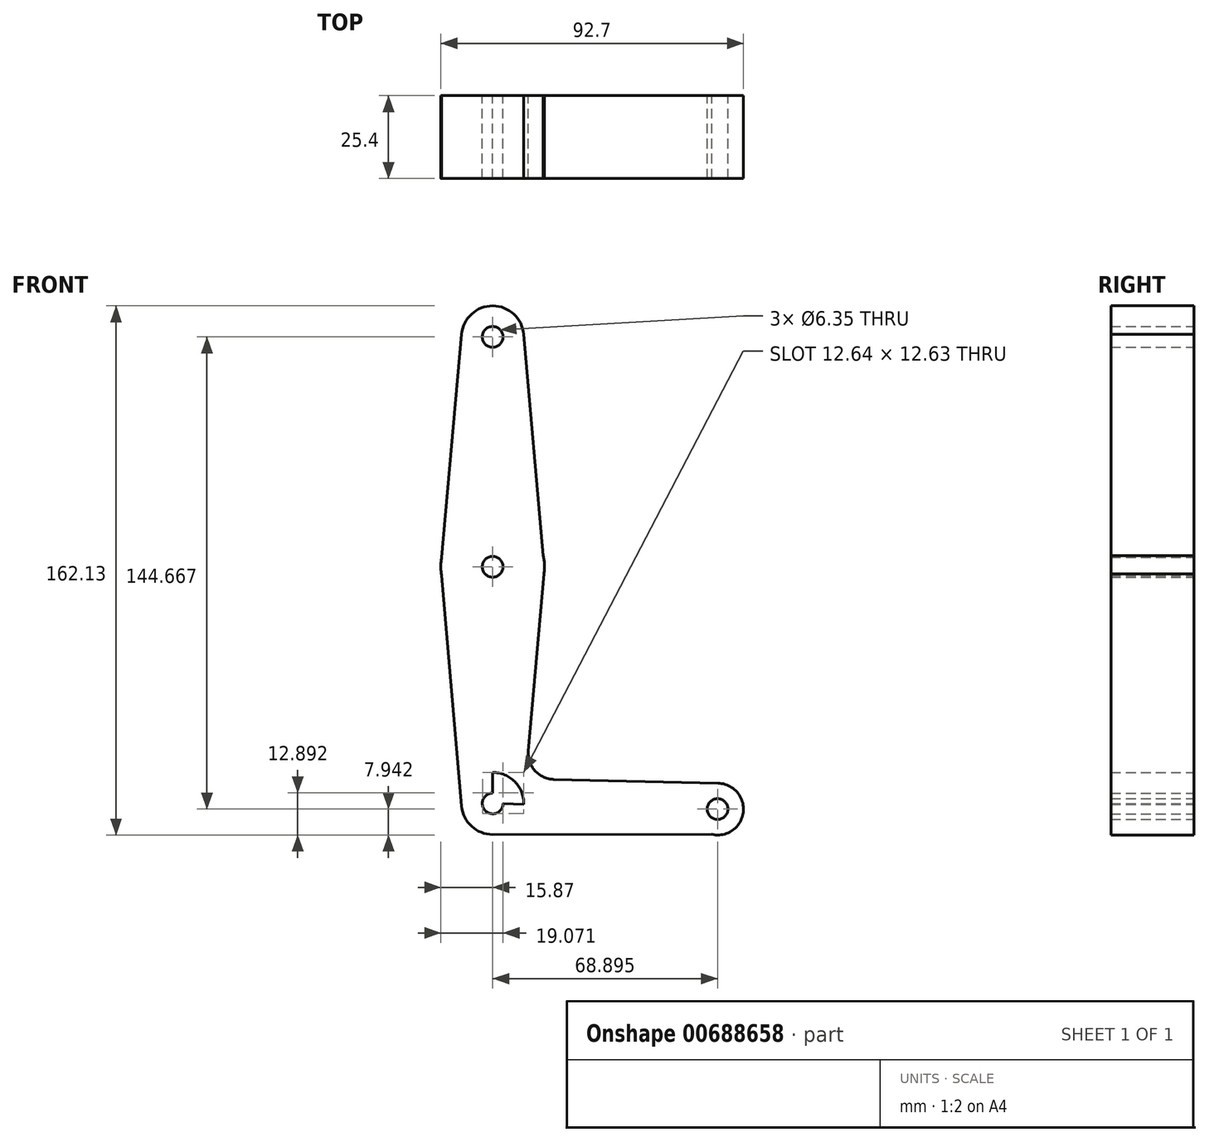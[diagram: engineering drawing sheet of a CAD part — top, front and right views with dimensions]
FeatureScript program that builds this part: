
annotation { "Feature Type Name" : "Feature", "Feature Type Description" : "" }
export const myFeature = defineFeature(function(context is Context, id is Id, definition is map)
    precondition{}
    {
        {
            var Q0;
            Q0=qCreatedBy(makeId("Front.planeOp"),FACE);
            var sketch = newSketch(context, id + "F0", { "sketchPlane" : qUnion([Q0])});
            skLineSegment(sketch, "E0", {"start": v(0, -72.52) * mm, "end": v(0, 70.4) * mm});
            skLineSegment(sketch, "E1", {"start": v(0, 70.4) * mm, "end": v(0, -72.52) * mm});
            skLineSegment(sketch, "E2", {"start": v(68.9, -74.26) * mm, "end": v(0, -72.52) * mm});
            skCircle(sketch, "E3", {"center": v(0, 70.4) * mm, "radius": 9.53 * mm});
            skCircle(sketch, "E4", {"center": v(0, 0) * mm, "radius": 15.88 * mm});
            skCircle(sketch, "E5", {"center": v(0, -72.52) * mm, "radius": 9.53 * mm});
            skCircle(sketch, "E6", {"center": v(68.9, -74.26) * mm, "radius": 7.94 * mm});
            skLineSegment(sketch, "E7", {"start": v(-9.48, 71.3) * mm, "end": v(-15.87, 0) * mm});
            skLineSegment(sketch, "E8", {"start": v(9.5, 71.15) * mm, "end": v(15.86, -0.58) * mm});
            skLineSegment(sketch, "E9", {"start": v(-15.87, 0) * mm, "end": v(-9.49, -73.34) * mm});
            skLineSegment(sketch, "E10", {"start": v(15.86, -0.58) * mm, "end": v(10.95, -56.5) * mm});
            skLineSegment(sketch, "E11", {"start": v(69.01, -66.32) * mm, "end": v(18.68, -65.14) * mm});
            skLineSegment(sketch, "E12", {"start": v(70.6, -82.01) * mm, "end": v(0, -82.04) * mm});
            skArc(sketch, "E13.filletArc", {"start": v(10.95, -56.5) * mm, "mid": v(12.94, -62.49) * mm, "end": v(18.68, -65.14) * mm});
            skCircle(sketch, "E14", {"center": v(0, 70.4) * mm, "radius": 3.18 * mm});
            skCircle(sketch, "E15", {"center": v(0, 0) * mm, "radius": 3.18 * mm});
            skCircle(sketch, "E16", {"center": v(0, -72.52) * mm, "radius": 3.18 * mm});
            skCircle(sketch, "E17", {"center": v(68.9, -74.26) * mm, "radius": 3.18 * mm});
            skText(sketch, "E18", { "text": "james collins, pd.1, 7.493", "fontName": "OpenSans-Regular.ttf"});
            const initialGuessF0  = {"E18": [0.05465, 0.06403, 1, 0, 0.02398]};
            skSetInitialGuess(sketch, initialGuessF0);
            skSolve(sketch);
        }
        {
            var Q0;
            Q0 = qSketchRegion(id + "F0", true);
            extrude(context, id + "F1", {"entities" : qUnion([Q0]), "depth" : 25.4 * mm, "offsetDistance" : 25.4 * mm});
        }
        {
            var Q0;
            Q0=makeQuery(id+"F1.opExtrude","SWEPT_BODY",BODY,{"disambiguationData":[OSD([sQuery(id+"F0.wireOp",EDGE,"E18.sketch_text.stroke-297"),sQuery(id+"F0.wireOp",EDGE,"E18.sketch_text.stroke-298"),sQuery(id+"F0.wireOp",EDGE,"E18.sketch_text.stroke-299"),sQuery(id+"F0.wireOp",EDGE,"E18.sketch_text.stroke-300"),sQuery(id+"F0.wireOp",EDGE,"E18.sketch_text.stroke-301"),sQuery(id+"F0.wireOp",EDGE,"E18.sketch_text.stroke-302"),sQuery(id+"F0.wireOp",EDGE,"E18.sketch_text.stroke-303"),sQuery(id+"F0.wireOp",EDGE,"E18.sketch_text.stroke-304")])]});
            deleteBodies(context, id + "F2", {"entities" : qUnion([Q0])});
        }
        {
            var Q0;
            Q0=makeQuery(id+"F1.opExtrude","SWEPT_BODY",BODY,{"disambiguationData":[OSD([sQuery(id+"F0.wireOp",EDGE,"E18.sketch_text.stroke-305"),sQuery(id+"F0.wireOp",EDGE,"E18.sketch_text.stroke-306"),sQuery(id+"F0.wireOp",EDGE,"E18.sketch_text.stroke-307"),sQuery(id+"F0.wireOp",EDGE,"E18.sketch_text.stroke-308"),sQuery(id+"F0.wireOp",EDGE,"E18.sketch_text.stroke-309"),sQuery(id+"F0.wireOp",EDGE,"E18.sketch_text.stroke-310"),sQuery(id+"F0.wireOp",EDGE,"E18.sketch_text.stroke-311"),sQuery(id+"F0.wireOp",EDGE,"E18.sketch_text.stroke-312"),sQuery(id+"F0.wireOp",EDGE,"E18.sketch_text.stroke-313"),sQuery(id+"F0.wireOp",EDGE,"E18.sketch_text.stroke-314"),sQuery(id+"F0.wireOp",EDGE,"E18.sketch_text.stroke-315"),sQuery(id+"F0.wireOp",EDGE,"E18.sketch_text.stroke-316"),sQuery(id+"F0.wireOp",EDGE,"E18.sketch_text.stroke-317"),sQuery(id+"F0.wireOp",EDGE,"E18.sketch_text.stroke-318"),sQuery(id+"F0.wireOp",EDGE,"E18.sketch_text.stroke-319"),sQuery(id+"F0.wireOp",EDGE,"E18.sketch_text.stroke-320"),sQuery(id+"F0.wireOp",EDGE,"E18.sketch_text.stroke-321")])]});
            var Q1;
            Q1=makeQuery(id+"F1.opExtrude","SWEPT_BODY",BODY,{"disambiguationData":[OSD([sQuery(id+"F0.wireOp",EDGE,"E18.sketch_text.stroke-290"),sQuery(id+"F0.wireOp",EDGE,"E18.sketch_text.stroke-291"),sQuery(id+"F0.wireOp",EDGE,"E18.sketch_text.stroke-292"),sQuery(id+"F0.wireOp",EDGE,"E18.sketch_text.stroke-293"),sQuery(id+"F0.wireOp",EDGE,"E18.sketch_text.stroke-294"),sQuery(id+"F0.wireOp",EDGE,"E18.sketch_text.stroke-295"),sQuery(id+"F0.wireOp",EDGE,"E18.sketch_text.stroke-296")])]});
            deleteBodies(context, id + "F3", {"entities" : qUnion([Q0, Q1])});
        }
        {
            var Q0;
            Q0=makeQuery(id+"F1.opExtrude","SWEPT_BODY",BODY,{"disambiguationData":[OSD([sQuery(id+"F0.wireOp",EDGE,"E18.sketch_text.stroke-348"),sQuery(id+"F0.wireOp",EDGE,"E18.sketch_text.stroke-349"),sQuery(id+"F0.wireOp",EDGE,"E18.sketch_text.stroke-350"),sQuery(id+"F0.wireOp",EDGE,"E18.sketch_text.stroke-351"),sQuery(id+"F0.wireOp",EDGE,"E18.sketch_text.stroke-352"),sQuery(id+"F0.wireOp",EDGE,"E18.sketch_text.stroke-353"),sQuery(id+"F0.wireOp",EDGE,"E18.sketch_text.stroke-354"),sQuery(id+"F0.wireOp",EDGE,"E18.sketch_text.stroke-355"),sQuery(id+"F0.wireOp",EDGE,"E18.sketch_text.stroke-356"),sQuery(id+"F0.wireOp",EDGE,"E18.sketch_text.stroke-357"),sQuery(id+"F0.wireOp",EDGE,"E18.sketch_text.stroke-358"),sQuery(id+"F0.wireOp",EDGE,"E18.sketch_text.stroke-359"),sQuery(id+"F0.wireOp",EDGE,"E18.sketch_text.stroke-360"),sQuery(id+"F0.wireOp",EDGE,"E18.sketch_text.stroke-361"),sQuery(id+"F0.wireOp",EDGE,"E18.sketch_text.stroke-362"),sQuery(id+"F0.wireOp",EDGE,"E18.sketch_text.stroke-363"),sQuery(id+"F0.wireOp",EDGE,"E18.sketch_text.stroke-364"),sQuery(id+"F0.wireOp",EDGE,"E18.sketch_text.stroke-365"),sQuery(id+"F0.wireOp",EDGE,"E18.sketch_text.stroke-366"),sQuery(id+"F0.wireOp",EDGE,"E18.sketch_text.stroke-367"),sQuery(id+"F0.wireOp",EDGE,"E18.sketch_text.stroke-368"),sQuery(id+"F0.wireOp",EDGE,"E18.sketch_text.stroke-369"),sQuery(id+"F0.wireOp",EDGE,"E18.sketch_text.stroke-370"),sQuery(id+"F0.wireOp",EDGE,"E18.sketch_text.stroke-371"),sQuery(id+"F0.wireOp",EDGE,"E18.sketch_text.stroke-372"),sQuery(id+"F0.wireOp",EDGE,"E18.sketch_text.stroke-373"),sQuery(id+"F0.wireOp",EDGE,"E18.sketch_text.stroke-374"),sQuery(id+"F0.wireOp",EDGE,"E18.sketch_text.stroke-375")])]});
            deleteBodies(context, id + "F4", {"entities" : qUnion([Q0])});
        }
        {
            var Q0;
            Q0=makeQuery(id+"F1.opExtrude","SWEPT_BODY",BODY,{"disambiguationData":[OSD([sQuery(id+"F0.wireOp",EDGE,"E18.sketch_text.stroke-322"),sQuery(id+"F0.wireOp",EDGE,"E18.sketch_text.stroke-323"),sQuery(id+"F0.wireOp",EDGE,"E18.sketch_text.stroke-324"),sQuery(id+"F0.wireOp",EDGE,"E18.sketch_text.stroke-325"),sQuery(id+"F0.wireOp",EDGE,"E18.sketch_text.stroke-326"),sQuery(id+"F0.wireOp",EDGE,"E18.sketch_text.stroke-327"),sQuery(id+"F0.wireOp",EDGE,"E18.sketch_text.stroke-328"),sQuery(id+"F0.wireOp",EDGE,"E18.sketch_text.stroke-329"),sQuery(id+"F0.wireOp",EDGE,"E18.sketch_text.stroke-330"),sQuery(id+"F0.wireOp",EDGE,"E18.sketch_text.stroke-331"),sQuery(id+"F0.wireOp",EDGE,"E18.sketch_text.stroke-332"),sQuery(id+"F0.wireOp",EDGE,"E18.sketch_text.stroke-333"),sQuery(id+"F0.wireOp",EDGE,"E18.sketch_text.stroke-334"),sQuery(id+"F0.wireOp",EDGE,"E18.sketch_text.stroke-335"),sQuery(id+"F0.wireOp",EDGE,"E18.sketch_text.stroke-336"),sQuery(id+"F0.wireOp",EDGE,"E18.sketch_text.stroke-337"),sQuery(id+"F0.wireOp",EDGE,"E18.sketch_text.stroke-338"),sQuery(id+"F0.wireOp",EDGE,"E18.sketch_text.stroke-339"),sQuery(id+"F0.wireOp",EDGE,"E18.sketch_text.stroke-340"),sQuery(id+"F0.wireOp",EDGE,"E18.sketch_text.stroke-341"),sQuery(id+"F0.wireOp",EDGE,"E18.sketch_text.stroke-342"),sQuery(id+"F0.wireOp",EDGE,"E18.sketch_text.stroke-343"),sQuery(id+"F0.wireOp",EDGE,"E18.sketch_text.stroke-344"),sQuery(id+"F0.wireOp",EDGE,"E18.sketch_text.stroke-345"),sQuery(id+"F0.wireOp",EDGE,"E18.sketch_text.stroke-346"),sQuery(id+"F0.wireOp",EDGE,"E18.sketch_text.stroke-347")])]});
            deleteBodies(context, id + "F5", {"entities" : qUnion([Q0])});
        }
        {
            var Q0;
            Q0=makeQuery(id+"F1.opExtrude","SWEPT_BODY",BODY,{"disambiguationData":[OSD([sQuery(id+"F0.wireOp",EDGE,"E18.sketch_text.stroke-283"),sQuery(id+"F0.wireOp",EDGE,"E18.sketch_text.stroke-284"),sQuery(id+"F0.wireOp",EDGE,"E18.sketch_text.stroke-285"),sQuery(id+"F0.wireOp",EDGE,"E18.sketch_text.stroke-286"),sQuery(id+"F0.wireOp",EDGE,"E18.sketch_text.stroke-287"),sQuery(id+"F0.wireOp",EDGE,"E18.sketch_text.stroke-288"),sQuery(id+"F0.wireOp",EDGE,"E18.sketch_text.stroke-289")])]});
            deleteBodies(context, id + "F6", {"entities" : qUnion([Q0])});
        }
        {
            var Q0;
            Q0=makeQuery(id+"F1.opExtrude","SWEPT_BODY",BODY,{"disambiguationData":[OSD([sQuery(id+"F0.wireOp",EDGE,"E18.sketch_text.stroke-0"),sQuery(id+"F0.wireOp",EDGE,"E18.sketch_text.stroke-1"),sQuery(id+"F0.wireOp",EDGE,"E18.sketch_text.stroke-2"),sQuery(id+"F0.wireOp",EDGE,"E18.sketch_text.stroke-3"),sQuery(id+"F0.wireOp",EDGE,"E18.sketch_text.stroke-4"),sQuery(id+"F0.wireOp",EDGE,"E18.sketch_text.stroke-5"),sQuery(id+"F0.wireOp",EDGE,"E18.sketch_text.stroke-6"),sQuery(id+"F0.wireOp",EDGE,"E18.sketch_text.stroke-7"),sQuery(id+"F0.wireOp",EDGE,"E18.sketch_text.stroke-8")])]});
            deleteBodies(context, id + "F7", {"entities" : qUnion([Q0])});
        }
        {
            var Q0;
            Q0=makeQuery(id+"F1.opExtrude","SWEPT_BODY",BODY,{"disambiguationData":[OSD([sQuery(id+"F0.wireOp",EDGE,"E18.sketch_text.stroke-9"),sQuery(id+"F0.wireOp",EDGE,"E18.sketch_text.stroke-10"),sQuery(id+"F0.wireOp",EDGE,"E18.sketch_text.stroke-11"),sQuery(id+"F0.wireOp",EDGE,"E18.sketch_text.stroke-12"),sQuery(id+"F0.wireOp",EDGE,"E18.sketch_text.stroke-13"),sQuery(id+"F0.wireOp",EDGE,"E18.sketch_text.stroke-14"),sQuery(id+"F0.wireOp",EDGE,"E18.sketch_text.stroke-15"),sQuery(id+"F0.wireOp",EDGE,"E18.sketch_text.stroke-16")])]});
            deleteBodies(context, id + "F8", {"entities" : qUnion([Q0])});
        }
        {
            var Q0;
            Q0=makeQuery(id+"F1.opExtrude","SWEPT_BODY",BODY,{"disambiguationData":[OSD([sQuery(id+"F0.wireOp",EDGE,"E18.sketch_text.stroke-17"),sQuery(id+"F0.wireOp",EDGE,"E18.sketch_text.stroke-18"),sQuery(id+"F0.wireOp",EDGE,"E18.sketch_text.stroke-19"),sQuery(id+"F0.wireOp",EDGE,"E18.sketch_text.stroke-20"),sQuery(id+"F0.wireOp",EDGE,"E18.sketch_text.stroke-21"),sQuery(id+"F0.wireOp",EDGE,"E18.sketch_text.stroke-22"),sQuery(id+"F0.wireOp",EDGE,"E18.sketch_text.stroke-23"),sQuery(id+"F0.wireOp",EDGE,"E18.sketch_text.stroke-24"),sQuery(id+"F0.wireOp",EDGE,"E18.sketch_text.stroke-25"),sQuery(id+"F0.wireOp",EDGE,"E18.sketch_text.stroke-26"),sQuery(id+"F0.wireOp",EDGE,"E18.sketch_text.stroke-27"),sQuery(id+"F0.wireOp",EDGE,"E18.sketch_text.stroke-28"),sQuery(id+"F0.wireOp",EDGE,"E18.sketch_text.stroke-29"),sQuery(id+"F0.wireOp",EDGE,"E18.sketch_text.stroke-30"),sQuery(id+"F0.wireOp",EDGE,"E18.sketch_text.stroke-31"),sQuery(id+"F0.wireOp",EDGE,"E18.sketch_text.stroke-32"),sQuery(id+"F0.wireOp",EDGE,"E18.sketch_text.stroke-33"),sQuery(id+"F0.wireOp",EDGE,"E18.sketch_text.stroke-34"),sQuery(id+"F0.wireOp",EDGE,"E18.sketch_text.stroke-35"),sQuery(id+"F0.wireOp",EDGE,"E18.sketch_text.stroke-36"),sQuery(id+"F0.wireOp",EDGE,"E18.sketch_text.stroke-37"),sQuery(id+"F0.wireOp",EDGE,"E18.sketch_text.stroke-38"),sQuery(id+"F0.wireOp",EDGE,"E18.sketch_text.stroke-39"),sQuery(id+"F0.wireOp",EDGE,"E18.sketch_text.stroke-40"),sQuery(id+"F0.wireOp",EDGE,"E18.sketch_text.stroke-41"),sQuery(id+"F0.wireOp",EDGE,"E18.sketch_text.stroke-42"),sQuery(id+"F0.wireOp",EDGE,"E18.sketch_text.stroke-43")])]});
            deleteBodies(context, id + "F9", {"entities" : qUnion([Q0])});
        }
        {
            var Q0;
            Q0=makeQuery(id+"F1.opExtrude","SWEPT_BODY",BODY,{"disambiguationData":[OSD([sQuery(id+"F0.wireOp",EDGE,"E18.sketch_text.stroke-72"),sQuery(id+"F0.wireOp",EDGE,"E18.sketch_text.stroke-73"),sQuery(id+"F0.wireOp",EDGE,"E18.sketch_text.stroke-74"),sQuery(id+"F0.wireOp",EDGE,"E18.sketch_text.stroke-75"),sQuery(id+"F0.wireOp",EDGE,"E18.sketch_text.stroke-76"),sQuery(id+"F0.wireOp",EDGE,"E18.sketch_text.stroke-77"),sQuery(id+"F0.wireOp",EDGE,"E18.sketch_text.stroke-78"),sQuery(id+"F0.wireOp",EDGE,"E18.sketch_text.stroke-79"),sQuery(id+"F0.wireOp",EDGE,"E18.sketch_text.stroke-80"),sQuery(id+"F0.wireOp",EDGE,"E18.sketch_text.stroke-81"),sQuery(id+"F0.wireOp",EDGE,"E18.sketch_text.stroke-82"),sQuery(id+"F0.wireOp",EDGE,"E18.sketch_text.stroke-83"),sQuery(id+"F0.wireOp",EDGE,"E18.sketch_text.stroke-84"),sQuery(id+"F0.wireOp",EDGE,"E18.sketch_text.stroke-85"),sQuery(id+"F0.wireOp",EDGE,"E18.sketch_text.stroke-86"),sQuery(id+"F0.wireOp",EDGE,"E18.sketch_text.stroke-87"),sQuery(id+"F0.wireOp",EDGE,"E18.sketch_text.stroke-88"),sQuery(id+"F0.wireOp",EDGE,"E18.sketch_text.stroke-89"),sQuery(id+"F0.wireOp",EDGE,"E18.sketch_text.stroke-90")])]});
            deleteBodies(context, id + "F10", {"entities" : qUnion([Q0])});
        }
        {
            var Q0;
            Q0=makeQuery(id+"F1.opExtrude","SWEPT_BODY",BODY,{"disambiguationData":[OSD([sQuery(id+"F0.wireOp",EDGE,"E18.sketch_text.stroke-44"),sQuery(id+"F0.wireOp",EDGE,"E18.sketch_text.stroke-45"),sQuery(id+"F0.wireOp",EDGE,"E18.sketch_text.stroke-46"),sQuery(id+"F0.wireOp",EDGE,"E18.sketch_text.stroke-47"),sQuery(id+"F0.wireOp",EDGE,"E18.sketch_text.stroke-48"),sQuery(id+"F0.wireOp",EDGE,"E18.sketch_text.stroke-49"),sQuery(id+"F0.wireOp",EDGE,"E18.sketch_text.stroke-50"),sQuery(id+"F0.wireOp",EDGE,"E18.sketch_text.stroke-51"),sQuery(id+"F0.wireOp",EDGE,"E18.sketch_text.stroke-52"),sQuery(id+"F0.wireOp",EDGE,"E18.sketch_text.stroke-53"),sQuery(id+"F0.wireOp",EDGE,"E18.sketch_text.stroke-54"),sQuery(id+"F0.wireOp",EDGE,"E18.sketch_text.stroke-55"),sQuery(id+"F0.wireOp",EDGE,"E18.sketch_text.stroke-56"),sQuery(id+"F0.wireOp",EDGE,"E18.sketch_text.stroke-57"),sQuery(id+"F0.wireOp",EDGE,"E18.sketch_text.stroke-58"),sQuery(id+"F0.wireOp",EDGE,"E18.sketch_text.stroke-59"),sQuery(id+"F0.wireOp",EDGE,"E18.sketch_text.stroke-60"),sQuery(id+"F0.wireOp",EDGE,"E18.sketch_text.stroke-61"),sQuery(id+"F0.wireOp",EDGE,"E18.sketch_text.stroke-62"),sQuery(id+"F0.wireOp",EDGE,"E18.sketch_text.stroke-63"),sQuery(id+"F0.wireOp",EDGE,"E18.sketch_text.stroke-64"),sQuery(id+"F0.wireOp",EDGE,"E18.sketch_text.stroke-65"),sQuery(id+"F0.wireOp",EDGE,"E18.sketch_text.stroke-66"),sQuery(id+"F0.wireOp",EDGE,"E18.sketch_text.stroke-67"),sQuery(id+"F0.wireOp",EDGE,"E18.sketch_text.stroke-68"),sQuery(id+"F0.wireOp",EDGE,"E18.sketch_text.stroke-69"),sQuery(id+"F0.wireOp",EDGE,"E18.sketch_text.stroke-70"),sQuery(id+"F0.wireOp",EDGE,"E18.sketch_text.stroke-71")])]});
            deleteBodies(context, id + "F11", {"entities" : qUnion([Q0])});
        }
        {
            var Q0;
            Q0=makeQuery(id+"F1.opExtrude","SWEPT_BODY",BODY,{"disambiguationData":[OSD([sQuery(id+"F0.wireOp",EDGE,"E18.sketch_text.stroke-91"),sQuery(id+"F0.wireOp",EDGE,"E18.sketch_text.stroke-92"),sQuery(id+"F0.wireOp",EDGE,"E18.sketch_text.stroke-93"),sQuery(id+"F0.wireOp",EDGE,"E18.sketch_text.stroke-94"),sQuery(id+"F0.wireOp",EDGE,"E18.sketch_text.stroke-95"),sQuery(id+"F0.wireOp",EDGE,"E18.sketch_text.stroke-96"),sQuery(id+"F0.wireOp",EDGE,"E18.sketch_text.stroke-97"),sQuery(id+"F0.wireOp",EDGE,"E18.sketch_text.stroke-98"),sQuery(id+"F0.wireOp",EDGE,"E18.sketch_text.stroke-99"),sQuery(id+"F0.wireOp",EDGE,"E18.sketch_text.stroke-100"),sQuery(id+"F0.wireOp",EDGE,"E18.sketch_text.stroke-101"),sQuery(id+"F0.wireOp",EDGE,"E18.sketch_text.stroke-102"),sQuery(id+"F0.wireOp",EDGE,"E18.sketch_text.stroke-103"),sQuery(id+"F0.wireOp",EDGE,"E18.sketch_text.stroke-104"),sQuery(id+"F0.wireOp",EDGE,"E18.sketch_text.stroke-105"),sQuery(id+"F0.wireOp",EDGE,"E18.sketch_text.stroke-106"),sQuery(id+"F0.wireOp",EDGE,"E18.sketch_text.stroke-107"),sQuery(id+"F0.wireOp",EDGE,"E18.sketch_text.stroke-108"),sQuery(id+"F0.wireOp",EDGE,"E18.sketch_text.stroke-109"),sQuery(id+"F0.wireOp",EDGE,"E18.sketch_text.stroke-110"),sQuery(id+"F0.wireOp",EDGE,"E18.sketch_text.stroke-111"),sQuery(id+"F0.wireOp",EDGE,"E18.sketch_text.stroke-112"),sQuery(id+"F0.wireOp",EDGE,"E18.sketch_text.stroke-113"),sQuery(id+"F0.wireOp",EDGE,"E18.sketch_text.stroke-114"),sQuery(id+"F0.wireOp",EDGE,"E18.sketch_text.stroke-115")])]});
            deleteBodies(context, id + "F12", {"entities" : qUnion([Q0])});
        }
        {
            var Q0;
            Q0=makeQuery(id+"F1.opExtrude","SWEPT_BODY",BODY,{"disambiguationData":[OSD([sQuery(id+"F0.wireOp",EDGE,"E18.sketch_text.stroke-116"),sQuery(id+"F0.wireOp",EDGE,"E18.sketch_text.stroke-117"),sQuery(id+"F0.wireOp",EDGE,"E18.sketch_text.stroke-118"),sQuery(id+"F0.wireOp",EDGE,"E18.sketch_text.stroke-119"),sQuery(id+"F0.wireOp",EDGE,"E18.sketch_text.stroke-120"),sQuery(id+"F0.wireOp",EDGE,"E18.sketch_text.stroke-121"),sQuery(id+"F0.wireOp",EDGE,"E18.sketch_text.stroke-122"),sQuery(id+"F0.wireOp",EDGE,"E18.sketch_text.stroke-123"),sQuery(id+"F0.wireOp",EDGE,"E18.sketch_text.stroke-124"),sQuery(id+"F0.wireOp",EDGE,"E18.sketch_text.stroke-125"),sQuery(id+"F0.wireOp",EDGE,"E18.sketch_text.stroke-126"),sQuery(id+"F0.wireOp",EDGE,"E18.sketch_text.stroke-127"),sQuery(id+"F0.wireOp",EDGE,"E18.sketch_text.stroke-128"),sQuery(id+"F0.wireOp",EDGE,"E18.sketch_text.stroke-129"),sQuery(id+"F0.wireOp",EDGE,"E18.sketch_text.stroke-130")])]});
            deleteBodies(context, id + "F13", {"entities" : qUnion([Q0])});
        }
        {
            var Q0;
            Q0=makeQuery(id+"F1.opExtrude","SWEPT_BODY",BODY,{"disambiguationData":[OSD([sQuery(id+"F0.wireOp",EDGE,"E18.sketch_text.stroke-131"),sQuery(id+"F0.wireOp",EDGE,"E18.sketch_text.stroke-132"),sQuery(id+"F0.wireOp",EDGE,"E18.sketch_text.stroke-133"),sQuery(id+"F0.wireOp",EDGE,"E18.sketch_text.stroke-134"),sQuery(id+"F0.wireOp",EDGE,"E18.sketch_text.stroke-135"),sQuery(id+"F0.wireOp",EDGE,"E18.sketch_text.stroke-136"),sQuery(id+"F0.wireOp",EDGE,"E18.sketch_text.stroke-137"),sQuery(id+"F0.wireOp",EDGE,"E18.sketch_text.stroke-138"),sQuery(id+"F0.wireOp",EDGE,"E18.sketch_text.stroke-139"),sQuery(id+"F0.wireOp",EDGE,"E18.sketch_text.stroke-140"),sQuery(id+"F0.wireOp",EDGE,"E18.sketch_text.stroke-141"),sQuery(id+"F0.wireOp",EDGE,"E18.sketch_text.stroke-142"),sQuery(id+"F0.wireOp",EDGE,"E18.sketch_text.stroke-143"),sQuery(id+"F0.wireOp",EDGE,"E18.sketch_text.stroke-144"),sQuery(id+"F0.wireOp",EDGE,"E18.sketch_text.stroke-145"),sQuery(id+"F0.wireOp",EDGE,"E18.sketch_text.stroke-146"),sQuery(id+"F0.wireOp",EDGE,"E18.sketch_text.stroke-147")])]});
            deleteBodies(context, id + "F14", {"entities" : qUnion([Q0])});
        }
        {
            var Q0;
            Q0=makeQuery(id+"F1.opExtrude","SWEPT_BODY",BODY,{"disambiguationData":[OSD([sQuery(id+"F0.wireOp",EDGE,"E18.sketch_text.stroke-148"),sQuery(id+"F0.wireOp",EDGE,"E18.sketch_text.stroke-149"),sQuery(id+"F0.wireOp",EDGE,"E18.sketch_text.stroke-150"),sQuery(id+"F0.wireOp",EDGE,"E18.sketch_text.stroke-151")])]});
            deleteBodies(context, id + "F15", {"entities" : qUnion([Q0])});
        }
        {
            var Q0;
            Q0=makeQuery(id+"F1.opExtrude","SWEPT_BODY",BODY,{"disambiguationData":[OSD([sQuery(id+"F0.wireOp",EDGE,"E18.sketch_text.stroke-152"),sQuery(id+"F0.wireOp",EDGE,"E18.sketch_text.stroke-153"),sQuery(id+"F0.wireOp",EDGE,"E18.sketch_text.stroke-154"),sQuery(id+"F0.wireOp",EDGE,"E18.sketch_text.stroke-155")])]});
            deleteBodies(context, id + "F16", {"entities" : qUnion([Q0])});
        }
        {
            var Q0;
            Q0=makeQuery(id+"F1.opExtrude","SWEPT_BODY",BODY,{"disambiguationData":[OSD([sQuery(id+"F0.wireOp",EDGE,"E18.sketch_text.stroke-156"),sQuery(id+"F0.wireOp",EDGE,"E18.sketch_text.stroke-157"),sQuery(id+"F0.wireOp",EDGE,"E18.sketch_text.stroke-158"),sQuery(id+"F0.wireOp",EDGE,"E18.sketch_text.stroke-159")])]});
            deleteBodies(context, id + "F17", {"entities" : qUnion([Q0])});
        }
        {
            var Q0;
            Q0=makeQuery(id+"F1.opExtrude","SWEPT_BODY",BODY,{"disambiguationData":[OSD([sQuery(id+"F0.wireOp",EDGE,"E18.sketch_text.stroke-160"),sQuery(id+"F0.wireOp",EDGE,"E18.sketch_text.stroke-161"),sQuery(id+"F0.wireOp",EDGE,"E18.sketch_text.stroke-162"),sQuery(id+"F0.wireOp",EDGE,"E18.sketch_text.stroke-163"),sQuery(id+"F0.wireOp",EDGE,"E18.sketch_text.stroke-164"),sQuery(id+"F0.wireOp",EDGE,"E18.sketch_text.stroke-165"),sQuery(id+"F0.wireOp",EDGE,"E18.sketch_text.stroke-166"),sQuery(id+"F0.wireOp",EDGE,"E18.sketch_text.stroke-167")])]});
            deleteBodies(context, id + "F18", {"entities" : qUnion([Q0])});
        }
        {
            var Q0;
            Q0=makeQuery(id+"F1.opExtrude","SWEPT_BODY",BODY,{"disambiguationData":[OSD([sQuery(id+"F0.wireOp",EDGE,"E18.sketch_text.stroke-168"),sQuery(id+"F0.wireOp",EDGE,"E18.sketch_text.stroke-169"),sQuery(id+"F0.wireOp",EDGE,"E18.sketch_text.stroke-170"),sQuery(id+"F0.wireOp",EDGE,"E18.sketch_text.stroke-171"),sQuery(id+"F0.wireOp",EDGE,"E18.sketch_text.stroke-172"),sQuery(id+"F0.wireOp",EDGE,"E18.sketch_text.stroke-173"),sQuery(id+"F0.wireOp",EDGE,"E18.sketch_text.stroke-174"),sQuery(id+"F0.wireOp",EDGE,"E18.sketch_text.stroke-175"),sQuery(id+"F0.wireOp",EDGE,"E18.sketch_text.stroke-176"),sQuery(id+"F0.wireOp",EDGE,"E18.sketch_text.stroke-177"),sQuery(id+"F0.wireOp",EDGE,"E18.sketch_text.stroke-178"),sQuery(id+"F0.wireOp",EDGE,"E18.sketch_text.stroke-179"),sQuery(id+"F0.wireOp",EDGE,"E18.sketch_text.stroke-180"),sQuery(id+"F0.wireOp",EDGE,"E18.sketch_text.stroke-181"),sQuery(id+"F0.wireOp",EDGE,"E18.sketch_text.stroke-182"),sQuery(id+"F0.wireOp",EDGE,"E18.sketch_text.stroke-183"),sQuery(id+"F0.wireOp",EDGE,"E18.sketch_text.stroke-184")])]});
            deleteBodies(context, id + "F19", {"entities" : qUnion([Q0])});
        }
        {
            var Q0;
            Q0=makeQuery(id+"F1.opExtrude","SWEPT_BODY",BODY,{"disambiguationData":[OSD([sQuery(id+"F0.wireOp",EDGE,"E18.sketch_text.stroke-185"),sQuery(id+"F0.wireOp",EDGE,"E18.sketch_text.stroke-186"),sQuery(id+"F0.wireOp",EDGE,"E18.sketch_text.stroke-187"),sQuery(id+"F0.wireOp",EDGE,"E18.sketch_text.stroke-188"),sQuery(id+"F0.wireOp",EDGE,"E18.sketch_text.stroke-189"),sQuery(id+"F0.wireOp",EDGE,"E18.sketch_text.stroke-190"),sQuery(id+"F0.wireOp",EDGE,"E18.sketch_text.stroke-191"),sQuery(id+"F0.wireOp",EDGE,"E18.sketch_text.stroke-192"),sQuery(id+"F0.wireOp",EDGE,"E18.sketch_text.stroke-193"),sQuery(id+"F0.wireOp",EDGE,"E18.sketch_text.stroke-194"),sQuery(id+"F0.wireOp",EDGE,"E18.sketch_text.stroke-195"),sQuery(id+"F0.wireOp",EDGE,"E18.sketch_text.stroke-196"),sQuery(id+"F0.wireOp",EDGE,"E18.sketch_text.stroke-197"),sQuery(id+"F0.wireOp",EDGE,"E18.sketch_text.stroke-198"),sQuery(id+"F0.wireOp",EDGE,"E18.sketch_text.stroke-199"),sQuery(id+"F0.wireOp",EDGE,"E18.sketch_text.stroke-200"),sQuery(id+"F0.wireOp",EDGE,"E18.sketch_text.stroke-201"),sQuery(id+"F0.wireOp",EDGE,"E18.sketch_text.stroke-202"),sQuery(id+"F0.wireOp",EDGE,"E18.sketch_text.stroke-203"),sQuery(id+"F0.wireOp",EDGE,"E18.sketch_text.stroke-204"),sQuery(id+"F0.wireOp",EDGE,"E18.sketch_text.stroke-205"),sQuery(id+"F0.wireOp",EDGE,"E18.sketch_text.stroke-206"),sQuery(id+"F0.wireOp",EDGE,"E18.sketch_text.stroke-207"),sQuery(id+"F0.wireOp",EDGE,"E18.sketch_text.stroke-208"),sQuery(id+"F0.wireOp",EDGE,"E18.sketch_text.stroke-209")])]});
            deleteBodies(context, id + "F20", {"entities" : qUnion([Q0])});
        }
        {
            var Q0;
            Q0=makeQuery(id+"F1.opExtrude","SWEPT_BODY",BODY,{"disambiguationData":[OSD([sQuery(id+"F0.wireOp",EDGE,"E18.sketch_text.stroke-210"),sQuery(id+"F0.wireOp",EDGE,"E18.sketch_text.stroke-211"),sQuery(id+"F0.wireOp",EDGE,"E18.sketch_text.stroke-212"),sQuery(id+"F0.wireOp",EDGE,"E18.sketch_text.stroke-213"),sQuery(id+"F0.wireOp",EDGE,"E18.sketch_text.stroke-214"),sQuery(id+"F0.wireOp",EDGE,"E18.sketch_text.stroke-215"),sQuery(id+"F0.wireOp",EDGE,"E18.sketch_text.stroke-216")])]});
            deleteBodies(context, id + "F21", {"entities" : qUnion([Q0])});
        }
        {
            var Q0;
            Q0=makeQuery(id+"F1.opExtrude","SWEPT_BODY",BODY,{"disambiguationData":[OSD([sQuery(id+"F0.wireOp",EDGE,"E18.sketch_text.stroke-217"),sQuery(id+"F0.wireOp",EDGE,"E18.sketch_text.stroke-218"),sQuery(id+"F0.wireOp",EDGE,"E18.sketch_text.stroke-219"),sQuery(id+"F0.wireOp",EDGE,"E18.sketch_text.stroke-220"),sQuery(id+"F0.wireOp",EDGE,"E18.sketch_text.stroke-221"),sQuery(id+"F0.wireOp",EDGE,"E18.sketch_text.stroke-222"),sQuery(id+"F0.wireOp",EDGE,"E18.sketch_text.stroke-223"),sQuery(id+"F0.wireOp",EDGE,"E18.sketch_text.stroke-224"),sQuery(id+"F0.wireOp",EDGE,"E18.sketch_text.stroke-225"),sQuery(id+"F0.wireOp",EDGE,"E18.sketch_text.stroke-226"),sQuery(id+"F0.wireOp",EDGE,"E18.sketch_text.stroke-227"),sQuery(id+"F0.wireOp",EDGE,"E18.sketch_text.stroke-228"),sQuery(id+"F0.wireOp",EDGE,"E18.sketch_text.stroke-229"),sQuery(id+"F0.wireOp",EDGE,"E18.sketch_text.stroke-230"),sQuery(id+"F0.wireOp",EDGE,"E18.sketch_text.stroke-231"),sQuery(id+"F0.wireOp",EDGE,"E18.sketch_text.stroke-232"),sQuery(id+"F0.wireOp",EDGE,"E18.sketch_text.stroke-233"),sQuery(id+"F0.wireOp",EDGE,"E18.sketch_text.stroke-234"),sQuery(id+"F0.wireOp",EDGE,"E18.sketch_text.stroke-235"),sQuery(id+"F0.wireOp",EDGE,"E18.sketch_text.stroke-236"),sQuery(id+"F0.wireOp",EDGE,"E18.sketch_text.stroke-237"),sQuery(id+"F0.wireOp",EDGE,"E18.sketch_text.stroke-238"),sQuery(id+"F0.wireOp",EDGE,"E18.sketch_text.stroke-239"),sQuery(id+"F0.wireOp",EDGE,"E18.sketch_text.stroke-240"),sQuery(id+"F0.wireOp",EDGE,"E18.sketch_text.stroke-241")])]});
            deleteBodies(context, id + "F22", {"entities" : qUnion([Q0])});
        }
        {
            var Q0;
            Q0=makeQuery(id+"F1.opExtrude","SWEPT_BODY",BODY,{"disambiguationData":[OSD([sQuery(id+"F0.wireOp",EDGE,"E18.sketch_text.stroke-242"),sQuery(id+"F0.wireOp",EDGE,"E18.sketch_text.stroke-243"),sQuery(id+"F0.wireOp",EDGE,"E18.sketch_text.stroke-244"),sQuery(id+"F0.wireOp",EDGE,"E18.sketch_text.stroke-245"),sQuery(id+"F0.wireOp",EDGE,"E18.sketch_text.stroke-246"),sQuery(id+"F0.wireOp",EDGE,"E18.sketch_text.stroke-247"),sQuery(id+"F0.wireOp",EDGE,"E18.sketch_text.stroke-248"),sQuery(id+"F0.wireOp",EDGE,"E18.sketch_text.stroke-249"),sQuery(id+"F0.wireOp",EDGE,"E18.sketch_text.stroke-250"),sQuery(id+"F0.wireOp",EDGE,"E18.sketch_text.stroke-251"),sQuery(id+"F0.wireOp",EDGE,"E18.sketch_text.stroke-252"),sQuery(id+"F0.wireOp",EDGE,"E18.sketch_text.stroke-253"),sQuery(id+"F0.wireOp",EDGE,"E18.sketch_text.stroke-254"),sQuery(id+"F0.wireOp",EDGE,"E18.sketch_text.stroke-255"),sQuery(id+"F0.wireOp",EDGE,"E18.sketch_text.stroke-256"),sQuery(id+"F0.wireOp",EDGE,"E18.sketch_text.stroke-257"),sQuery(id+"F0.wireOp",EDGE,"E18.sketch_text.stroke-258"),sQuery(id+"F0.wireOp",EDGE,"E18.sketch_text.stroke-259"),sQuery(id+"F0.wireOp",EDGE,"E18.sketch_text.stroke-260"),sQuery(id+"F0.wireOp",EDGE,"E18.sketch_text.stroke-261"),sQuery(id+"F0.wireOp",EDGE,"E18.sketch_text.stroke-262"),sQuery(id+"F0.wireOp",EDGE,"E18.sketch_text.stroke-263"),sQuery(id+"F0.wireOp",EDGE,"E18.sketch_text.stroke-264"),sQuery(id+"F0.wireOp",EDGE,"E18.sketch_text.stroke-265")])]});
            deleteBodies(context, id + "F23", {"entities" : qUnion([Q0])});
        }
        {
            var Q0;
            Q0=makeQuery(id+"F1.opExtrude","SWEPT_BODY",BODY,{"disambiguationData":[OSD([sQuery(id+"F0.wireOp",EDGE,"E18.sketch_text.stroke-266"),sQuery(id+"F0.wireOp",EDGE,"E18.sketch_text.stroke-267"),sQuery(id+"F0.wireOp",EDGE,"E18.sketch_text.stroke-268"),sQuery(id+"F0.wireOp",EDGE,"E18.sketch_text.stroke-269"),sQuery(id+"F0.wireOp",EDGE,"E18.sketch_text.stroke-270"),sQuery(id+"F0.wireOp",EDGE,"E18.sketch_text.stroke-271"),sQuery(id+"F0.wireOp",EDGE,"E18.sketch_text.stroke-272"),sQuery(id+"F0.wireOp",EDGE,"E18.sketch_text.stroke-273")])]});
            deleteBodies(context, id + "F24", {"entities" : qUnion([Q0])});
        }
        {
            var Q0;
            Q0=makeQuery(id+"F1.opExtrude","SWEPT_BODY",BODY,{"disambiguationData":[OSD([sQuery(id+"F0.wireOp",EDGE,"E18.sketch_text.stroke-274"),sQuery(id+"F0.wireOp",EDGE,"E18.sketch_text.stroke-275"),sQuery(id+"F0.wireOp",EDGE,"E18.sketch_text.stroke-276"),sQuery(id+"F0.wireOp",EDGE,"E18.sketch_text.stroke-277"),sQuery(id+"F0.wireOp",EDGE,"E18.sketch_text.stroke-278"),sQuery(id+"F0.wireOp",EDGE,"E18.sketch_text.stroke-279"),sQuery(id+"F0.wireOp",EDGE,"E18.sketch_text.stroke-280"),sQuery(id+"F0.wireOp",EDGE,"E18.sketch_text.stroke-281"),sQuery(id+"F0.wireOp",EDGE,"E18.sketch_text.stroke-282")])]});
            deleteBodies(context, id + "F25", {"entities" : qUnion([Q0])});
        }
    });
